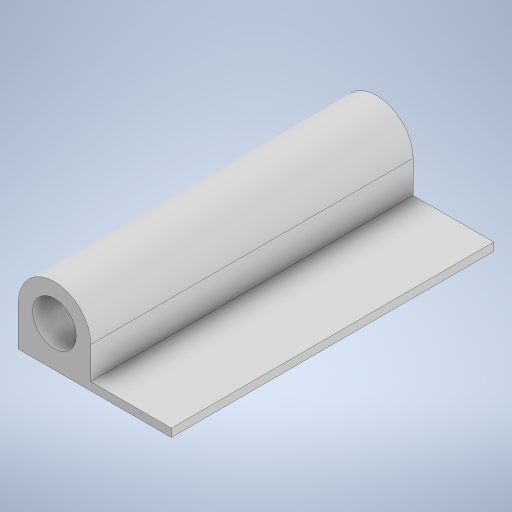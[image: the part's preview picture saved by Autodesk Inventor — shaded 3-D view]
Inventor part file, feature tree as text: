
AUTODESK INVENTOR PART (.ipt)
format: ipt  version: 2023 (Build 270158000, 158)  size: 237,568 bytes
history: native  units: in
note: dims shown in document units (in); Inventor stores cm internally (conversion verified against a paired STEP export)
features: extrude x1, thicken_offset x1, sketch x1
ambient origin geometry x8: Origin, YZ Plane, XZ Plane, XY Plane, X Axis, Y Axis, Z Axis, Center Point
bodies: Solid1 (feature_tree)
feature tree (3):
  extrude  "Extrusion1"  Depth=0.3543in
  thicken_offset  "Thicken1"
  sketch  "Sketch1"  dims[d1=0.0394in d2=0.1969in d3=0.1969in d4=0.0787in d5=0.3937in d6=1.5748in d7=0.0in d8=0.0079in d9=0.0079in d11=0.3543in]
